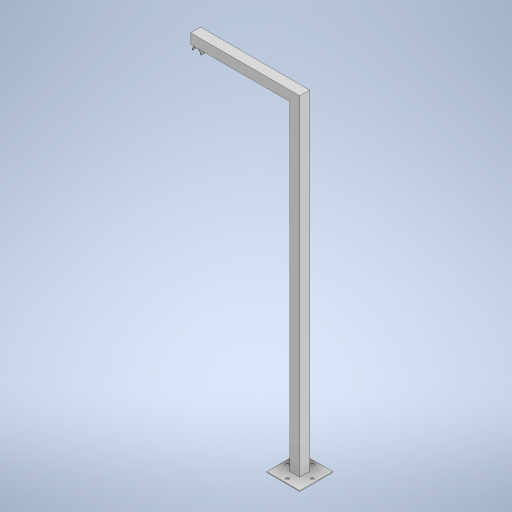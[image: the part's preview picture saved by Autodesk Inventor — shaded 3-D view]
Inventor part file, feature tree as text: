
AUTODESK INVENTOR PART (.ipt)
format: ipt  version: 2024 (Build 280153000, 153)  size: 290,816 bytes
history: native  units: mm
features: extrude x5, sketch x5, other x1
ambient origin geometry x8: Origin, YZ Plane, XZ Plane, XY Plane, X Axis, Y Axis, Z Axis, Center Point
bodies: Body1 (feature_tree)
feature tree (11):
  other  "Sólido1"
  extrude  "Extrusión1"  Depth=200.0mm
  extrude  "Extrusión2"  Depth=60.0mm
  extrude  "Extrusión3"  Depth=70.0mm
  extrude  "Extrusión4"  Depth=2000.0mm TaperAngle=0.0deg
  extrude  "Extrusión5"  Depth=60.0mm
  sketch  "Boceto1"  dims[d0=200.0mm d1=200.0mm]
  sketch  "Boceto2"  dims[d2=5.0mm d3=0.0mm d4=60.0mm]
  sketch  "Boceto3"  dims[d5=60.0mm d6=70.0mm]
  sketch  "Boceto4"  dims[d7=70.0mm d8=2000.0mm d9=0.0mm]
  sketch  "Boceto5"  dims[d10=60.0mm d11=60.0mm d12=600.0mm d13=0.0mm d14=50.0mm d15=35.0mm d16=26.0mm d17=55.0mm d18=60.0mm d19=0.0mm d20=18.5mm d21=75.0mm d22=40.0mm d24=360.0deg d26=10.0mm d27=0.0mm]
